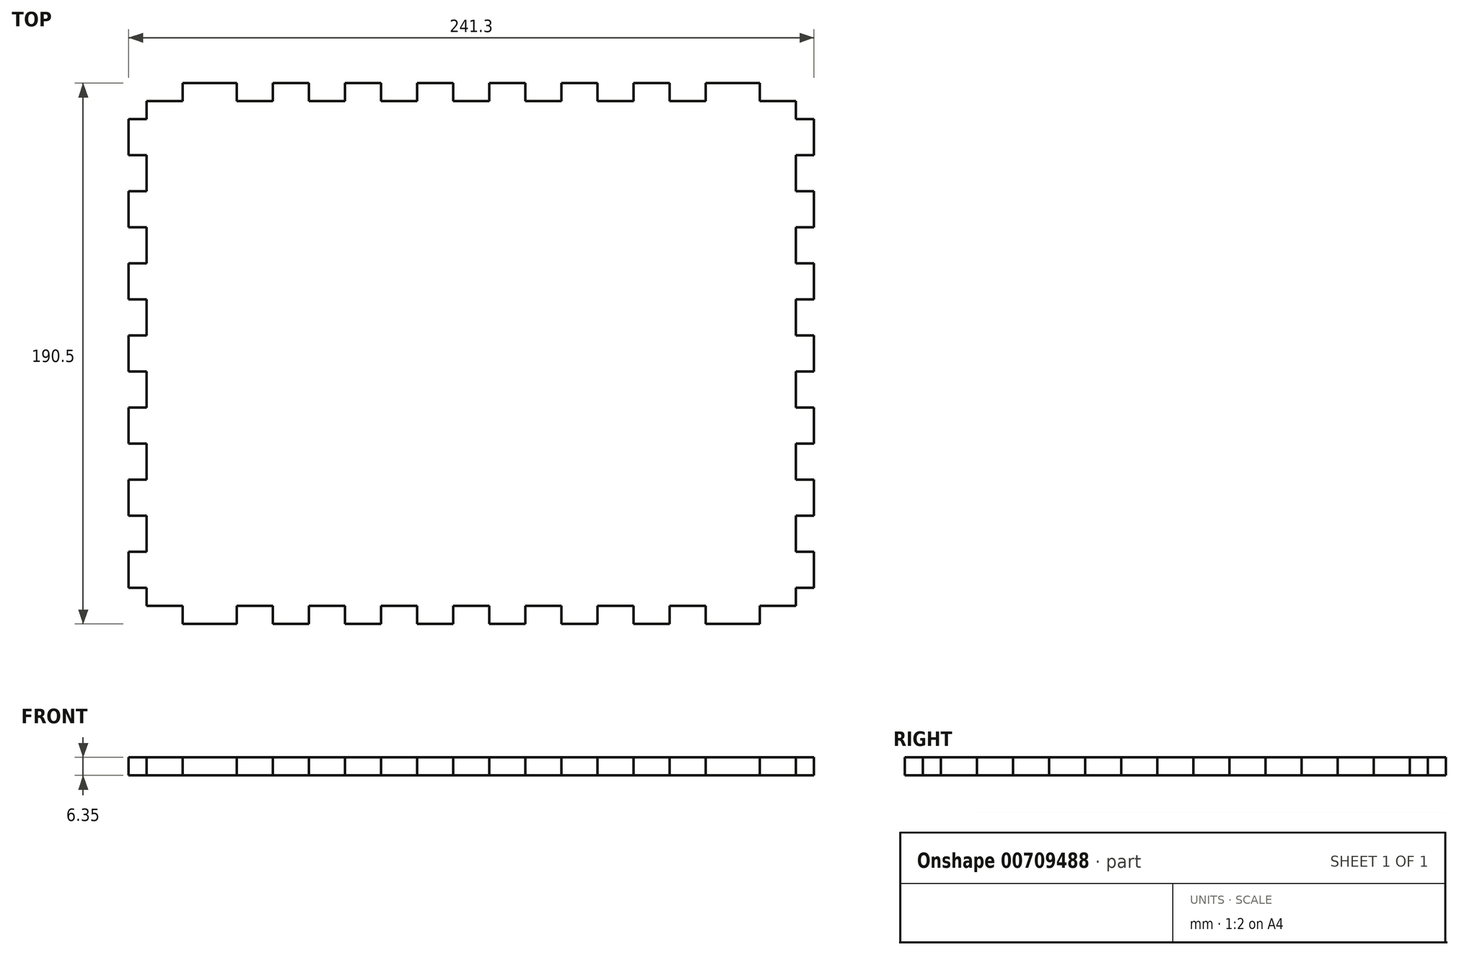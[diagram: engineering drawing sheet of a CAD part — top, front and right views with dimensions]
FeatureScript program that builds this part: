
annotation { "Feature Type Name" : "Feature", "Feature Type Description" : "" }
export const myFeature = defineFeature(function(context is Context, id is Id, definition is map)
    precondition{}
    {
        {
            var Q0;
            Q0=qCreatedBy(makeId("Top.planeOp"),FACE);
            var sketch = newSketch(context, id + "F0", { "sketchPlane" : qUnion([Q0])});
            skLineSegment(sketch, "E0.bottom", {"start": v(19.05, 0) * mm, "end": v(38.1, 0) * mm});
            skLineSegment(sketch, "E0.left", {"start": v(0, -12.7) * mm, "end": v(0, -25.4) * mm});
            skLineSegment(sketch, "E1", {"start": v(6.35, -6.35) * mm, "end": v(19.05, -6.35) * mm});
            skLineSegment(sketch, "E2", {"start": v(19.05, -6.35) * mm, "end": v(19.05, 0) * mm});
            skLineSegment(sketch, "E3", {"start": v(38.1, 0) * mm, "end": v(38.1, -6.35) * mm});
            skLineSegment(sketch, "E4", {"start": v(38.1, -6.35) * mm, "end": v(50.8, -6.35) * mm});
            skLineSegment(sketch, "E5", {"start": v(50.8, -6.35) * mm, "end": v(50.8, 0) * mm});
            skLineSegment(sketch, "E6", {"start": v(50.8, 0) * mm, "end": v(63.5, 0) * mm});
            skLineSegment(sketch, "E7", {"start": v(63.5, 0) * mm, "end": v(63.5, -6.35) * mm});
            skLineSegment(sketch, "E8", {"start": v(63.5, -6.35) * mm, "end": v(76.2, -6.35) * mm});
            skLineSegment(sketch, "E9", {"start": v(76.2, -6.35) * mm, "end": v(76.2, 0) * mm});
            skLineSegment(sketch, "E10", {"start": v(76.2, 0) * mm, "end": v(88.9, 0) * mm});
            skLineSegment(sketch, "E11", {"start": v(88.9, 0) * mm, "end": v(88.9, -6.35) * mm});
            skLineSegment(sketch, "E12", {"start": v(88.9, -6.35) * mm, "end": v(101.6, -6.35) * mm});
            skLineSegment(sketch, "E13", {"start": v(101.6, -6.35) * mm, "end": v(101.6, 0) * mm});
            skLineSegment(sketch, "E14.trimOffspring", {"start": v(101.6, 0) * mm, "end": v(114.3, 0) * mm});
            skLineSegment(sketch, "E15", {"start": v(114.3, 0) * mm, "end": v(114.3, -6.35) * mm});
            skLineSegment(sketch, "E16", {"start": v(114.3, -6.35) * mm, "end": v(127, -6.35) * mm});
            skLineSegment(sketch, "E17", {"start": v(127, -6.35) * mm, "end": v(127, 0) * mm});
            skLineSegment(sketch, "E18", {"start": v(127, 0) * mm, "end": v(139.7, 0) * mm});
            skLineSegment(sketch, "E19", {"start": v(139.7, 0) * mm, "end": v(139.7, -6.35) * mm});
            skLineSegment(sketch, "E20", {"start": v(139.7, -6.35) * mm, "end": v(152.4, -6.35) * mm});
            skLineSegment(sketch, "E21", {"start": v(152.4, -6.35) * mm, "end": v(152.4, 0) * mm});
            skLineSegment(sketch, "E22", {"start": v(152.4, 0) * mm, "end": v(165.1, 0) * mm});
            skLineSegment(sketch, "E23", {"start": v(165.1, 0) * mm, "end": v(165.1, -6.35) * mm});
            skLineSegment(sketch, "E24", {"start": v(165.1, -6.35) * mm, "end": v(177.8, -6.35) * mm});
            skLineSegment(sketch, "E25", {"start": v(177.8, -6.35) * mm, "end": v(177.8, 0) * mm});
            skLineSegment(sketch, "E26", {"start": v(177.8, 0) * mm, "end": v(190.5, 0) * mm});
            skLineSegment(sketch, "E27", {"start": v(190.5, 0) * mm, "end": v(190.5, -6.35) * mm});
            skLineSegment(sketch, "E28", {"start": v(190.5, -6.35) * mm, "end": v(203.2, -6.35) * mm});
            skLineSegment(sketch, "E29", {"start": v(203.2, -6.35) * mm, "end": v(203.2, 0) * mm});
            skLineSegment(sketch, "E30.trimOffspring", {"start": v(203.2, 0) * mm, "end": v(222.25, 0) * mm});
            skLineSegment(sketch, "E31", {"start": v(222.25, 0) * mm, "end": v(222.25, -6.35) * mm});
            skLineSegment(sketch, "E32", {"start": v(222.25, -6.35) * mm, "end": v(234.95, -6.35) * mm});
            skPoint(sketch, "E33.orphan", {"position": v(241.3, 0) * mm});
            skPoint(sketch, "E34.orphan", {"position": v(0, 0) * mm});
            skLineSegment(sketch, "E35", {"start": v(6.35, -6.35) * mm, "end": v(6.35, -12.7) * mm});
            skLineSegment(sketch, "E36", {"start": v(6.35, -12.7) * mm, "end": v(0, -12.7) * mm});
            skLineSegment(sketch, "E37", {"start": v(0, -25.4) * mm, "end": v(6.35, -25.4) * mm});
            skLineSegment(sketch, "E38", {"start": v(6.35, -25.4) * mm, "end": v(6.35, -38.1) * mm});
            skLineSegment(sketch, "E39", {"start": v(6.35, -38.1) * mm, "end": v(0, -38.1) * mm});
            skLineSegment(sketch, "E40", {"start": v(0, -38.1) * mm, "end": v(0, -50.8) * mm});
            skLineSegment(sketch, "E41", {"start": v(0, -50.8) * mm, "end": v(6.35, -50.8) * mm});
            skLineSegment(sketch, "E42", {"start": v(6.35, -50.8) * mm, "end": v(6.35, -63.5) * mm});
            skLineSegment(sketch, "E43", {"start": v(6.35, -63.5) * mm, "end": v(0, -63.5) * mm});
            skLineSegment(sketch, "E44", {"start": v(0, -63.5) * mm, "end": v(0, -76.2) * mm});
            skLineSegment(sketch, "E45", {"start": v(0, -76.2) * mm, "end": v(6.35, -76.2) * mm});
            skLineSegment(sketch, "E46", {"start": v(6.35, -76.2) * mm, "end": v(6.35, -88.9) * mm});
            skLineSegment(sketch, "E47", {"start": v(6.35, -88.9) * mm, "end": v(0, -88.9) * mm});
            skLineSegment(sketch, "E48", {"start": v(0, -88.9) * mm, "end": v(0, -101.6) * mm});
            skLineSegment(sketch, "E49", {"start": v(0, -101.6) * mm, "end": v(6.35, -101.6) * mm});
            skLineSegment(sketch, "E50", {"start": v(6.35, -101.6) * mm, "end": v(6.35, -114.3) * mm});
            skLineSegment(sketch, "E51", {"start": v(6.35, -114.3) * mm, "end": v(0, -114.3) * mm});
            skLineSegment(sketch, "E52.trimOffspring", {"start": v(0, -114.3) * mm, "end": v(0, -127) * mm});
            skLineSegment(sketch, "E53", {"start": v(0, -127) * mm, "end": v(6.35, -127) * mm});
            skLineSegment(sketch, "E54", {"start": v(6.35, -127) * mm, "end": v(6.35, -139.7) * mm});
            skLineSegment(sketch, "E55", {"start": v(6.35, -139.7) * mm, "end": v(0, -139.7) * mm});
            skLineSegment(sketch, "E56", {"start": v(0, -139.7) * mm, "end": v(0, -152.4) * mm});
            skLineSegment(sketch, "E57", {"start": v(0, -152.4) * mm, "end": v(6.35, -152.4) * mm});
            skLineSegment(sketch, "E58", {"start": v(6.35, -152.4) * mm, "end": v(6.35, -165.1) * mm});
            skLineSegment(sketch, "E59", {"start": v(6.35, -165.1) * mm, "end": v(0, -165.1) * mm});
            skLineSegment(sketch, "E60", {"start": v(0, -165.1) * mm, "end": v(0, -177.8) * mm});
            skLineSegment(sketch, "E61", {"start": v(0, -177.8) * mm, "end": v(6.35, -177.8) * mm});
            skLineSegment(sketch, "E62", {"start": v(6.35, -177.8) * mm, "end": v(6.35, -177.8) * mm});
            skPoint(sketch, "E63.orphan", {"position": v(0, -190.5) * mm});
            skLineSegment(sketch, "E64", {"start": v(120.65, -6.35) * mm, "end": v(120.65, -43.1) * mm, "construction": true});
            skLineSegment(sketch, "E65.MirrorCS", {"start": v(234.95, -6.35) * mm, "end": v(234.95, -12.7) * mm});
            skLineSegment(sketch, "E66.MirrorCS", {"start": v(234.95, -12.7) * mm, "end": v(241.3, -12.7) * mm});
            skLineSegment(sketch, "E67.MirrorCS", {"start": v(241.3, -12.7) * mm, "end": v(241.3, -25.4) * mm});
            skLineSegment(sketch, "E68.MirrorCS", {"start": v(241.3, -25.4) * mm, "end": v(234.95, -25.4) * mm});
            skLineSegment(sketch, "E69.MirrorCS", {"start": v(234.95, -25.4) * mm, "end": v(234.95, -38.1) * mm});
            skLineSegment(sketch, "E70.MirrorCS", {"start": v(234.95, -38.1) * mm, "end": v(241.3, -38.1) * mm});
            skLineSegment(sketch, "E71.MirrorCS", {"start": v(241.3, -38.1) * mm, "end": v(241.3, -50.8) * mm});
            skLineSegment(sketch, "E72.MirrorCS", {"start": v(241.3, -50.8) * mm, "end": v(234.95, -50.8) * mm});
            skLineSegment(sketch, "E73.MirrorCS", {"start": v(234.95, -50.8) * mm, "end": v(234.95, -63.5) * mm});
            skLineSegment(sketch, "E74.MirrorCS", {"start": v(234.95, -63.5) * mm, "end": v(241.3, -63.5) * mm});
            skLineSegment(sketch, "E75.MirrorCS", {"start": v(241.3, -63.5) * mm, "end": v(241.3, -76.2) * mm});
            skLineSegment(sketch, "E76.MirrorCS", {"start": v(241.3, -76.2) * mm, "end": v(234.95, -76.2) * mm});
            skLineSegment(sketch, "E77.MirrorCS", {"start": v(234.95, -76.2) * mm, "end": v(234.95, -88.9) * mm});
            skLineSegment(sketch, "E78.MirrorCS", {"start": v(234.95, -88.9) * mm, "end": v(241.3, -88.9) * mm});
            skLineSegment(sketch, "E79.MirrorCS", {"start": v(241.3, -88.9) * mm, "end": v(241.3, -101.6) * mm});
            skLineSegment(sketch, "E80.MirrorCS", {"start": v(241.3, -101.6) * mm, "end": v(234.95, -101.6) * mm});
            skLineSegment(sketch, "E81.MirrorCS", {"start": v(234.95, -101.6) * mm, "end": v(234.95, -114.3) * mm});
            skLineSegment(sketch, "E82.MirrorCS", {"start": v(234.95, -114.3) * mm, "end": v(241.3, -114.3) * mm});
            skLineSegment(sketch, "E83.MirrorCS", {"start": v(241.3, -114.3) * mm, "end": v(241.3, -127) * mm});
            skLineSegment(sketch, "E84.MirrorCS", {"start": v(241.3, -127) * mm, "end": v(234.95, -127) * mm});
            skLineSegment(sketch, "E85.MirrorCS", {"start": v(234.95, -127) * mm, "end": v(234.95, -139.7) * mm});
            skLineSegment(sketch, "E86.MirrorCS", {"start": v(234.95, -139.7) * mm, "end": v(241.3, -139.7) * mm});
            skLineSegment(sketch, "E87.MirrorCS", {"start": v(241.3, -139.7) * mm, "end": v(241.3, -152.4) * mm});
            skLineSegment(sketch, "E88.MirrorCS", {"start": v(241.3, -152.4) * mm, "end": v(234.95, -152.4) * mm});
            skLineSegment(sketch, "E89.MirrorCS", {"start": v(234.95, -152.4) * mm, "end": v(234.95, -165.1) * mm});
            skLineSegment(sketch, "E90.MirrorCS", {"start": v(234.95, -165.1) * mm, "end": v(241.3, -165.1) * mm});
            skLineSegment(sketch, "E91.MirrorCS", {"start": v(241.3, -165.1) * mm, "end": v(241.3, -177.8) * mm});
            skLineSegment(sketch, "E92.MirrorCS", {"start": v(241.3, -177.8) * mm, "end": v(234.95, -177.8) * mm});
            skLineSegment(sketch, "E93.MirrorCS", {"start": v(234.95, -177.8) * mm, "end": v(234.95, -177.8) * mm});
            skLineSegment(sketch, "E94", {"start": v(0, -95.25) * mm, "end": v(59.62, -95.25) * mm, "construction": true});
            skLineSegment(sketch, "E95.MirrorCS", {"start": v(6.35, -184.15) * mm, "end": v(19.05, -184.15) * mm});
            skLineSegment(sketch, "E96.MirrorCS", {"start": v(19.05, -184.15) * mm, "end": v(19.05, -190.5) * mm});
            skLineSegment(sketch, "E97.MirrorCS", {"start": v(19.05, -190.5) * mm, "end": v(38.1, -190.5) * mm});
            skLineSegment(sketch, "E98.MirrorCS", {"start": v(38.1, -190.5) * mm, "end": v(38.1, -184.15) * mm});
            skLineSegment(sketch, "E99.MirrorCS", {"start": v(38.1, -184.15) * mm, "end": v(50.8, -184.15) * mm});
            skLineSegment(sketch, "E100.MirrorCS", {"start": v(50.8, -184.15) * mm, "end": v(50.8, -190.5) * mm});
            skLineSegment(sketch, "E101.MirrorCS", {"start": v(50.8, -190.5) * mm, "end": v(63.5, -190.5) * mm});
            skLineSegment(sketch, "E102.MirrorCS", {"start": v(63.5, -190.5) * mm, "end": v(63.5, -184.15) * mm});
            skLineSegment(sketch, "E103.MirrorCS", {"start": v(63.5, -184.15) * mm, "end": v(76.2, -184.15) * mm});
            skLineSegment(sketch, "E104.MirrorCS", {"start": v(76.2, -184.15) * mm, "end": v(76.2, -190.5) * mm});
            skLineSegment(sketch, "E105.MirrorCS", {"start": v(76.2, -190.5) * mm, "end": v(88.9, -190.5) * mm});
            skLineSegment(sketch, "E106.MirrorCS", {"start": v(88.9, -190.5) * mm, "end": v(88.9, -184.15) * mm});
            skLineSegment(sketch, "E107.MirrorCS", {"start": v(88.9, -184.15) * mm, "end": v(101.6, -184.15) * mm});
            skLineSegment(sketch, "E108.MirrorCS", {"start": v(101.6, -184.15) * mm, "end": v(101.6, -190.5) * mm});
            skLineSegment(sketch, "E109.MirrorCS", {"start": v(101.6, -190.5) * mm, "end": v(114.3, -190.5) * mm});
            skLineSegment(sketch, "E110.MirrorCS", {"start": v(114.3, -190.5) * mm, "end": v(114.3, -184.15) * mm});
            skLineSegment(sketch, "E111.MirrorCS", {"start": v(114.3, -184.15) * mm, "end": v(127, -184.15) * mm});
            skLineSegment(sketch, "E112.MirrorCS", {"start": v(127, -184.15) * mm, "end": v(127, -190.5) * mm});
            skLineSegment(sketch, "E113.MirrorCS", {"start": v(127, -190.5) * mm, "end": v(139.7, -190.5) * mm});
            skLineSegment(sketch, "E114.MirrorCS", {"start": v(139.7, -190.5) * mm, "end": v(139.7, -184.15) * mm});
            skLineSegment(sketch, "E115.MirrorCS", {"start": v(139.7, -184.15) * mm, "end": v(152.4, -184.15) * mm});
            skLineSegment(sketch, "E116.MirrorCS", {"start": v(152.4, -184.15) * mm, "end": v(152.4, -190.5) * mm});
            skLineSegment(sketch, "E117.MirrorCS", {"start": v(152.4, -190.5) * mm, "end": v(165.1, -190.5) * mm});
            skLineSegment(sketch, "E118.MirrorCS", {"start": v(165.1, -190.5) * mm, "end": v(165.1, -184.15) * mm});
            skLineSegment(sketch, "E119.MirrorCS", {"start": v(165.1, -184.15) * mm, "end": v(177.8, -184.15) * mm});
            skLineSegment(sketch, "E120.MirrorCS", {"start": v(177.8, -184.15) * mm, "end": v(177.8, -190.5) * mm});
            skLineSegment(sketch, "E121.MirrorCS", {"start": v(177.8, -190.5) * mm, "end": v(190.5, -190.5) * mm});
            skLineSegment(sketch, "E122.MirrorCS", {"start": v(190.5, -190.5) * mm, "end": v(190.5, -184.15) * mm});
            skLineSegment(sketch, "E123.MirrorCS", {"start": v(190.5, -184.15) * mm, "end": v(203.2, -184.15) * mm});
            skLineSegment(sketch, "E124.MirrorCS", {"start": v(203.2, -184.15) * mm, "end": v(203.2, -190.5) * mm});
            skLineSegment(sketch, "E125.MirrorCS", {"start": v(203.2, -190.5) * mm, "end": v(222.25, -190.5) * mm});
            skLineSegment(sketch, "E126.MirrorCS", {"start": v(222.25, -190.5) * mm, "end": v(222.25, -184.15) * mm});
            skLineSegment(sketch, "E127.MirrorCS", {"start": v(222.25, -184.15) * mm, "end": v(234.95, -184.15) * mm});
            skLineSegment(sketch, "E128", {"start": v(6.35, -177.8) * mm, "end": v(6.35, -184.15) * mm});
            skLineSegment(sketch, "E129", {"start": v(234.95, -177.8) * mm, "end": v(234.95, -184.15) * mm});
            skSolve(sketch);
        }
        {
            var Q0;
            Q0=makeQuery(id+"F0.imprint","IMPRINT",FACE,{"disambiguationData":[TD([[makeQuery(id+"F0.imprint","IMPRINT",EDGE,{"derivedFrom":sQuery(id+"F0.wireOp",EDGE,"E1")}),-1.0]])]});
            extrude(context, id + "F1", {"entities" : qUnion([Q0]), "depth" : 6.35 * mm, "offsetDistance" : 25.4 * mm});
        }
    });
